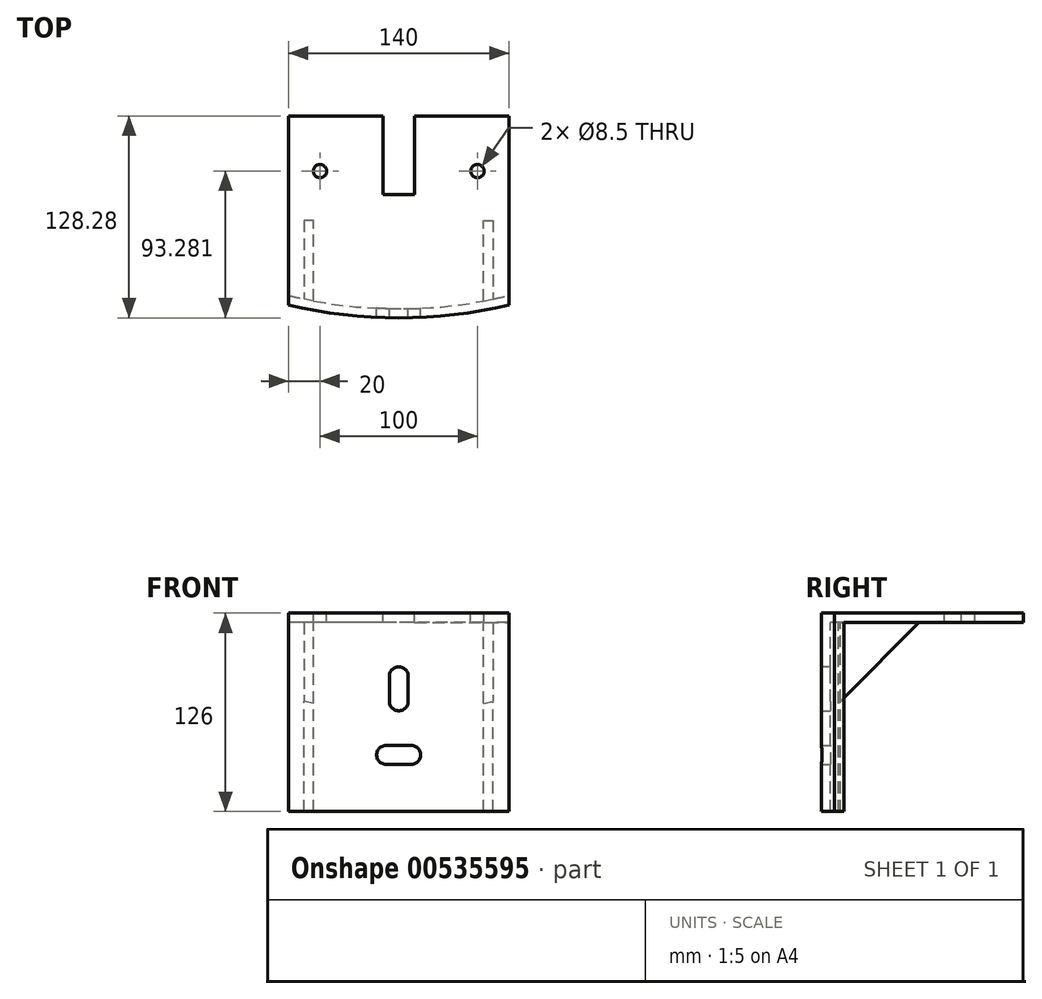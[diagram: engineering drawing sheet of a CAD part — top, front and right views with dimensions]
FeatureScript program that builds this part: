
annotation { "Feature Type Name" : "Feature", "Feature Type Description" : "" }
export const myFeature = defineFeature(function(context is Context, id is Id, definition is map)
    precondition{}
    {
        {
            var Q0;
            Q0=qCreatedBy(makeId("Top.planeOp"),FACE);
            var sketch = newSketch(context, id + "F0", { "sketchPlane" : qUnion([Q0])});
            skCircle(sketch, "E0", {"center": v(0, 0) * mm, "radius": 300 * mm});
            skLineSegment(sketch, "E1", {"start": v(0, 0) * mm, "end": v(0, -300) * mm, "construction": true});
            skLineSegment(sketch, "E2", {"start": v(0, -221.72) * mm, "end": v(10, -221.72) * mm});
            skLineSegment(sketch, "E3", {"start": v(10, -221.72) * mm, "end": v(10, -171.72) * mm});
            skLineSegment(sketch, "E4", {"start": v(10, -171.72) * mm, "end": v(70, -171.72) * mm});
            skLineSegment(sketch, "E5", {"start": v(70, -171.72) * mm, "end": v(70, -291.72) * mm});
            skLineSegment(sketch, "E6.MirrorCS", {"start": v(-70, -171.72) * mm, "end": v(-70, -291.72) * mm});
            skLineSegment(sketch, "E7.MirrorCS", {"start": v(-10, -171.72) * mm, "end": v(-70, -171.72) * mm});
            skLineSegment(sketch, "E8.MirrorCS", {"start": v(0, -221.72) * mm, "end": v(-10, -221.72) * mm});
            skLineSegment(sketch, "E9.MirrorCS", {"start": v(-10, -221.72) * mm, "end": v(-10, -171.72) * mm});
            skPoint(sketch, "E10", {"position": v(50, -206.72) * mm});
            skCircle(sketch, "E11", {"center": v(50, -206.72) * mm, "radius": 4.25 * mm});
            skCircle(sketch, "E12.MirrorC", {"center": v(-50, -206.72) * mm, "radius": 4.25 * mm});
            skSolve(sketch);
        }
        {
            var Q0;
            Q0=makeQuery(id+"F0.imprint","IMPRINT",FACE,{"disambiguationData":[TD([[makeQuery(id+"F0.imprint","IMPRINT",EDGE,{"derivedFrom":sQuery(id+"F0.wireOp",EDGE,"E2")}),-1.0]])]});
            extrude(context, id + "F1", {"entities" : qUnion([Q0]), "depth" : -6 * mm, "offsetDistance" : 25 * mm});
        }
        {
            var Q0;
            Q0=makeQuery(id+"F1.opExtrude","CAP_FACE",FACE,{"disambiguationData":[OSD([sQuery(id+"F0.wireOp",EDGE,"E0"),sQuery(id+"F0.wireOp",EDGE,"E2"),sQuery(id+"F0.wireOp",EDGE,"E3"),sQuery(id+"F0.wireOp",EDGE,"E4"),sQuery(id+"F0.wireOp",EDGE,"E5"),sQuery(id+"F0.wireOp",EDGE,"E6.MirrorCS"),sQuery(id+"F0.wireOp",EDGE,"E7.MirrorCS"),sQuery(id+"F0.wireOp",EDGE,"E8.MirrorCS"),sQuery(id+"F0.wireOp",EDGE,"E9.MirrorCS")])],"isStart":false});
            var sketch = newSketch(context, id + "F2", { "sketchPlane" : qUnion([Q0])});
            skArc(sketch, "E13", {"start": v(70, 285.72) * mm, "mid": v(0, 294.17) * mm, "end": v(-70, 285.72) * mm});
            skLineSegment(sketch, "E14", {"start": v(-70, 291.72) * mm, "end": v(-70, 285.72) * mm, "construction": true});
            skLineSegment(sketch, "E15", {"start": v(54, 237.99) * mm, "end": v(60, 237.99) * mm});
            skLineSegment(sketch, "E16", {"start": v(60, 237.99) * mm, "end": v(60, 287.99) * mm});
            skLineSegment(sketch, "E17", {"start": v(54, 237.99) * mm, "end": v(54, 289.17) * mm});
            skLineSegment(sketch, "E18", {"start": v(0, 221.72) * mm, "end": v(0, 300) * mm, "construction": true});
            skLineSegment(sketch, "E19.MirrorCS", {"start": v(-54, 237.99) * mm, "end": v(-60, 237.99) * mm});
            skLineSegment(sketch, "E20.MirrorCS", {"start": v(-54, 237.99) * mm, "end": v(-54, 289.17) * mm});
            skLineSegment(sketch, "E21.MirrorCS", {"start": v(-60, 237.99) * mm, "end": v(-60, 287.99) * mm});
            skSolve(sketch);
        }
        {
            var Q0;
            Q0=makeQuery(id+"F2.imprint","IMPRINT",FACE,{"disambiguationData":[TD([[makeQuery(id+"F2.imprint","IMPRINT",EDGE,{"derivedFrom":sQuery(id+"F2.wireOp",EDGE,"E19.MirrorCS")}),-1.0]])]});
            var Q1;
            {var subQ7=makeQuery(id+"F1.opExtrude","CAP_EDGE",EDGE,{"disambiguationData":[OSD([sQuery(id+"F0.wireOp",EDGE,"E0")])],"isStart":false});Q1=makeQuery(id+"F2.imprint","IMPRINT",FACE,{"disambiguationData":[TD([[makeQuery(id+"F2.imprint","IMPRINT",EDGE,{"derivedFrom":subQ7}),-1.0]])]});}
            var Q2;
            Q2=makeQuery(id+"F2.imprint","IMPRINT",FACE,{"disambiguationData":[TD([[makeQuery(id+"F2.imprint","IMPRINT",EDGE,{"derivedFrom":sQuery(id+"F2.wireOp",EDGE,"E15")}),1.0]])]});
            extrude(context, id + "F3", {"entities" : qUnion([Q0, Q1, Q2]), "operationType" : NewBodyOperationType.ADD, "depth" : 120 * mm, "offsetDistance" : 25 * mm});
        }
        {
            var Q0;
            Q0=makeQuery(id+"F3.opExtrude","SWEPT_FACE",FACE,{"disambiguationData":[OSD([sQuery(id+"F2.wireOp",EDGE,"E16")])]});
            var sketch = newSketch(context, id + "F4", { "sketchPlane" : qUnion([Q0])});
            skLineSegment(sketch, "E22", {"start": v(-237.99, -6) * mm, "end": v(-287.99, -56) * mm});
            skSolve(sketch);
        }
        {
            var Q0;
            {var subQ0=sQuery(id+"F4.wireOp",EDGE,"E22");Q0=makeQuery(id+"F4.imprint","IMPRINT",FACE,{"disambiguationData":[TD([[makeQuery(id+"F4.imprint","IMPRINT",EDGE,{"derivedFrom":subQ0}),1.0]])]});}
            var Q1;
            Q1=makeQuery(id+"F3.opExtrude","SWEPT_FACE",FACE,{"disambiguationData":[OSD([sQuery(id+"F2.wireOp",EDGE,"E21.MirrorCS")])]});
            var Q2;
            Q2=makeQuery(id+"F1.opExtrude","SWEPT_BODY",BODY,{"disambiguationData":[OSD([sQuery(id+"F0.wireOp",EDGE,"E0"),sQuery(id+"F0.wireOp",EDGE,"E2"),sQuery(id+"F0.wireOp",EDGE,"E3"),sQuery(id+"F0.wireOp",EDGE,"E4"),sQuery(id+"F0.wireOp",EDGE,"E5"),sQuery(id+"F0.wireOp",EDGE,"E6.MirrorCS"),sQuery(id+"F0.wireOp",EDGE,"E7.MirrorCS"),sQuery(id+"F0.wireOp",EDGE,"E8.MirrorCS"),sQuery(id+"F0.wireOp",EDGE,"E9.MirrorCS")])]});
            extrude(context, id + "F5", {"entities" : qUnion([Q0]), "operationType" : NewBodyOperationType.REMOVE, "endBound" : BoundingType.UP_TO_SURFACE, "oppositeDirection" : true, "depth" : 25 * mm, "endBoundEntityFace" : qUnion([Q1]), "endBoundEntityBody" : qUnion([Q2]), "offsetDistance" : 25 * mm});
        }
        {
            var Q0;
            Q0=makeQuery(id+"F3.opExtrude","CAP_FACE",FACE,{"disambiguationData":[OSD([sQuery(id+"F0.wireOp",EDGE,"E0"),sQuery(id+"F0.wireOp",EDGE,"E5"),sQuery(id+"F0.wireOp",EDGE,"E6.MirrorCS"),sQuery(id+"F2.wireOp",EDGE,"E13"),sQuery(id+"F2.wireOp",EDGE,"E15"),sQuery(id+"F2.wireOp",EDGE,"E16"),sQuery(id+"F2.wireOp",EDGE,"E17"),sQuery(id+"F2.wireOp",EDGE,"E19.MirrorCS"),sQuery(id+"F2.wireOp",EDGE,"E20.MirrorCS"),sQuery(id+"F2.wireOp",EDGE,"E21.MirrorCS")])],"isStart":false});
            var sketch = newSketch(context, id + "F6", { "sketchPlane" : qUnion([Q0])});
            skLineSegment(sketch, "E23", {"start": v(54, 289.17) * mm, "end": v(60, 287.99) * mm});
            skLineSegment(sketch, "E24", {"start": v(-54, 289.17) * mm, "end": v(-60, 287.99) * mm});
            skSolve(sketch);
        }
        {
            var Q0;
            Q0=makeQuery(id+"F6.imprint","IMPRINT",FACE,{"disambiguationData":[TD([[makeQuery(id+"F6.imprint","IMPRINT",EDGE,{"derivedFrom":sQuery(id+"F6.wireOp",EDGE,"E24")}),1.0]])]});
            var Q1;
            Q1=makeQuery(id+"F6.imprint","IMPRINT",FACE,{"disambiguationData":[TD([[makeQuery(id+"F6.imprint","IMPRINT",EDGE,{"derivedFrom":sQuery(id+"F6.wireOp",EDGE,"E23")}),-1.0]])]});
            var Q2;
            {var subQ0=sQuery(id+"F2.wireOp",EDGE,"E16");Q2=makeQuery(id+"F5.boolean.opBoolean","COPY",FACE,{"disambiguationData":[TD([makeQuery(id+"F3.opExtrude","SWEPT_FACE",FACE,{"disambiguationData":[OSD([subQ0])]})])],"derivedFrom":makeQuery(id+"F5.opExtrude","SWEPT_FACE",FACE,{"disambiguationData":[OSD([sQuery(id+"F4.wireOp",EDGE,"E22")])]})});}
            extrude(context, id + "F7", {"entities" : qUnion([Q0, Q1]), "operationType" : NewBodyOperationType.REMOVE, "endBound" : BoundingType.UP_TO_SURFACE, "oppositeDirection" : true, "depth" : 25 * mm, "endBoundEntityFace" : qUnion([Q2]), "offsetDistance" : 25 * mm});
        }
        {
            var Q0;
            Q0=qCreatedBy(makeId("Front.planeOp"),FACE);
            var sketch = newSketch(context, id + "F8", { "sketchPlane" : qUnion([Q0])});
            skLineSegment(sketch, "E25", {"start": v(0, 0) * mm, "end": v(0, -172.39) * mm, "construction": true});
            skArc(sketch, "E26", {"start": v(6, -40) * mm, "mid": v(0, -34) * mm, "end": v(-6, -40) * mm});
            skLineSegment(sketch, "E27", {"start": v(6, -40) * mm, "end": v(6, -48) * mm});
            skLineSegment(sketch, "E28", {"start": v(-6, -40) * mm, "end": v(-6, -48) * mm});
            skLineSegment(sketch, "E29", {"start": v(6, -48) * mm, "end": v(-6, -48) * mm, "construction": true});
            skLineSegment(sketch, "E30.MirrorCS", {"start": v(6, -56) * mm, "end": v(6, -48) * mm});
            skLineSegment(sketch, "E31.MirrorCS", {"start": v(-6, -56) * mm, "end": v(-6, -48) * mm});
            skArc(sketch, "E32.MirrorCS", {"start": v(6, -56) * mm, "mid": v(0, -62) * mm, "end": v(-6, -56) * mm});
            skLineSegment(sketch, "E33", {"start": v(0, -84) * mm, "end": v(8, -84) * mm});
            skArc(sketch, "E34", {"start": v(8, -96) * mm, "mid": v(14, -90) * mm, "end": v(8, -84) * mm});
            skLineSegment(sketch, "E35", {"start": v(8, -96) * mm, "end": v(0, -96) * mm});
            skLineSegment(sketch, "E36.MirrorCS", {"start": v(0, -84) * mm, "end": v(-8, -84) * mm});
            skLineSegment(sketch, "E37.MirrorCS", {"start": v(-8, -96) * mm, "end": v(0, -96) * mm});
            skArc(sketch, "E38.MirrorCS", {"start": v(-8, -96) * mm, "mid": v(-14, -90) * mm, "end": v(-8, -84) * mm});
            skSolve(sketch);
        }
        {
            var Q0;
            Q0=makeQuery(id+"F8.imprint","IMPRINT",FACE,{"disambiguationData":[TD([[makeQuery(id+"F8.imprint","IMPRINT",EDGE,{"derivedFrom":sQuery(id+"F8.wireOp",EDGE,"E33")}),-1.0]])]});
            var Q1;
            Q1=makeQuery(id+"F8.imprint","IMPRINT",FACE,{"disambiguationData":[TD([[makeQuery(id+"F8.imprint","IMPRINT",EDGE,{"derivedFrom":sQuery(id+"F8.wireOp",EDGE,"E26")}),1.0]])]});
            extrude(context, id + "F9", {"entities" : qUnion([Q0, Q1]), "operationType" : NewBodyOperationType.REMOVE, "endBound" : BoundingType.THROUGH_ALL, "depth" : 25 * mm, "offsetDistance" : 25 * mm});
        }
    });
